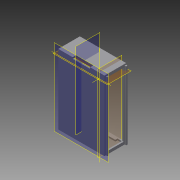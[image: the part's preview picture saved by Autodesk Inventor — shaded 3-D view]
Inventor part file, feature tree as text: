
AUTODESK INVENTOR PART (.ipt)
format: ipt  version: 2015 (Build 190159000, 159)  size: 260,096 bytes
history: native  units: mm
features: sketch x14, projected_geometry x11, extrude x9, sweep x1, plane x1, mirror x1
ambient origin geometry x8: Origin, YZ Plane, XZ Plane, XY Plane, X Axis, Y Axis, Z Axis, Center Point
bodies: Solid1 (feature_tree)
feature tree (37):
  sketch  "Sketch1"  dims[d0=2.5mm d1=20.0mm d3=49.0mm d4=20.0mm d6=58.0mm]
  extrude  "Extrusion1"  Depth=20.0mm
  extrude  "Extrusion2"  Depth=3.5mm
  sketch  "Sketch4"  dims[d14=3.5mm d15=2.0mm]
  sketch  "Sketch5"  dims[d16=2.0mm d17=0.0mm d18=2.0mm]
  sketch  "3D Sketch1"
  sweep  "Sweep2"
  extrude  "Extrusion3"  Depth=2.0mm
  extrude  "Extrusion5"  Depth=2.0mm
  extrude  "Extrusion6"  TaperAngle=0.0deg  [1 undecoded]
  sketch  "Sketch12"  dims[d41=5.0mm d42=2.0mm d43=0.0mm]
  sketch  "Sketch13"  dims[d44=5.0mm d45=5.0mm]
  extrude  "Extrusion10"  Depth=2.0mm TaperAngle=0.0deg
  extrude  "Extrusion11"  Depth=20.0mm
  extrude  "Extrusion12"  Depth=2.0mm TaperAngle=0.0deg
  plane  "Work Plane1"
  mirror  "Mirror1"
  extrude  "Extrusion13"  Depth=5.0mm
  sketch  "Sketch2"  dims[d9=10.0mm d10=0.0mm d11=3.5mm]
  sketch  "Sketch3"  dims[d12=27.0mm d13=3.5mm]
  projected_geometry  "Projected Loop1"
  projected_geometry  "Projected Loop2"
  projected_geometry  "Projected Loop3"
  projected_geometry  "Projected Loop4"
  sketch  "3D Sketch2"
  sketch  "Sketch6"  dims[d19=30.0mm d23=0.0mm d24=0.0mm]
  sketch  "Sketch8"  dims[d25=5.0mm d26=2.0mm d27=0.0mm]
  sketch  "Sketch9"  dims[d39=20.0mm d40=20.0mm]
  projected_geometry  "Projected Loop5"
  projected_geometry  "Projected Loop6"
  projected_geometry  "Projected Loop7"
  projected_geometry  "Projected Loop8"
  projected_geometry  "Projected Loop11"
  projected_geometry  "Projected Loop12"
  projected_geometry  "Projected Loop13"
  sketch  "Sketch14"  dims[d46=5.0mm]
  sketch  "Sketch15"  dims[d47=5.0mm d48=4.0mm d49=0.0mm d67=2.0mm d68=2.0mm d69=3.5mm d70=2.0mm d72=8.0mm d73=2.0mm d74=10.0mm d75=0.0mm d76=10.0mm d77=0.0mm d78=2.0mm d79=2.0mm d80=2.0mm d81=2.0mm d82=0.0mm d83=0.0mm d84=0.0mm d85=24.0mm d86=94.5mm d87=0.0mm d88=2.0mm d89=0.0mm]
note: 1 required parameter value undecoded (feature->parameter linkage not recoverable at this tier; creation-order binding heuristic only, values carry confidence <= 0.55)
